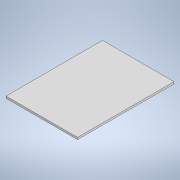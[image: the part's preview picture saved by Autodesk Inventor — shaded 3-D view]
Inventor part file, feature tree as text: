
AUTODESK INVENTOR PART (.ipt)
format: ipt  version: 2020 (Build 240168000, 168)  size: 89,600 bytes
history: native  units: in
note: dims shown in document units (in); Inventor stores cm internally (conversion verified against a paired STEP export)
features: extrude x1, sketch x1
ambient origin geometry x8: Origin, YZ Plane, XZ Plane, XY Plane, X Axis, Y Axis, Z Axis, Center Point
bodies: Solid1 (feature_tree)
feature tree (2):
  extrude  "Extrusion1"  Depth=2.8426in
  sketch  "Sketch1"  dims[d0=3.8319in d1=2.8426in d2=0.0787in d3=0.0in]
